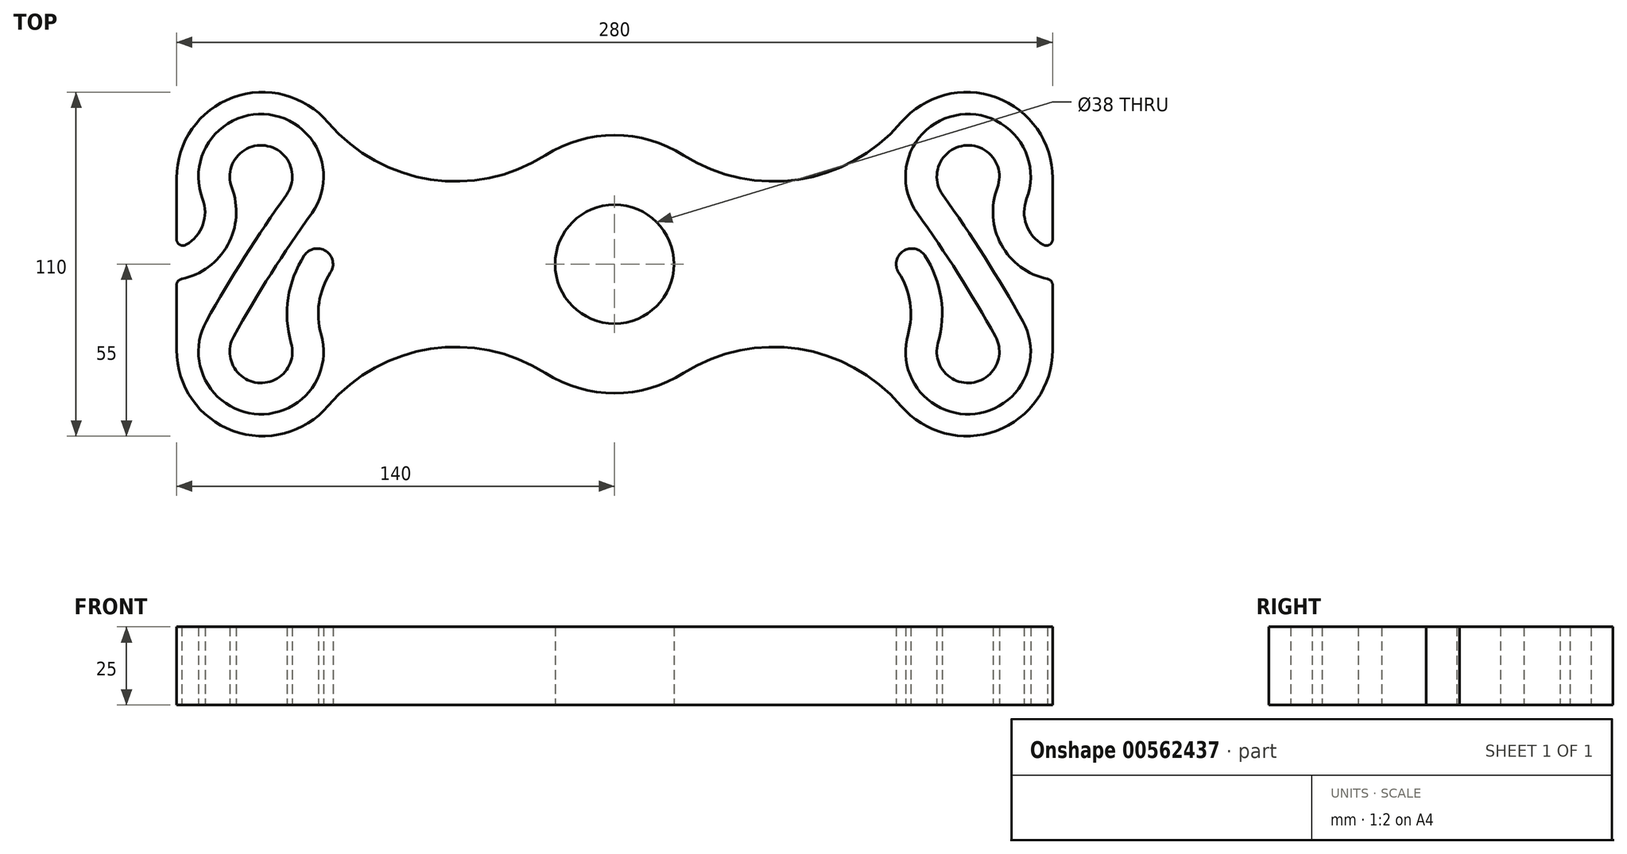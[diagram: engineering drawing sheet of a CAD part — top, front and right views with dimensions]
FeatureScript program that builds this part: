
annotation { "Feature Type Name" : "Feature", "Feature Type Description" : "" }
export const myFeature = defineFeature(function(context is Context, id is Id, definition is map)
    precondition{}
    {
        {
            var Q0;
            Q0=qCreatedBy(makeId("Top.planeOp"),FACE);
            var sketch = newSketch(context, id + "F0", { "sketchPlane" : qUnion([Q0])});
            skLineSegment(sketch, "E0.bottom", {"start": v(0, 0) * mm, "end": v(280, 0) * mm, "construction": true});
            skLineSegment(sketch, "E0.top", {"start": v(0, 110) * mm, "end": v(280, 110) * mm, "construction": true});
            skLineSegment(sketch, "E0.left", {"start": v(0, 0) * mm, "end": v(0, 110) * mm, "construction": true});
            skLineSegment(sketch, "E0.right", {"start": v(280, 0) * mm, "end": v(280, 110) * mm, "construction": true});
            skArc(sketch, "E1", {"start": v(140, 74) * mm, "mid": v(121, 55) * mm, "end": v(140, 36) * mm});
            skPoint(sketch, "E1.centerSnap0", {"position": v(0, 55) * mm});
            skPoint(sketch, "E1.centerSnap1", {"position": v(140, 110) * mm});
            skCircle(sketch, "E2", {"center": v(140, 55) * mm, "radius": 55 * mm, "construction": true});
            skLineSegment(sketch, "E3", {"start": v(0, 55) * mm, "end": v(280, 55) * mm, "construction": true});
            skArc(sketch, "E4", {"start": v(48.44, 100.32) * mm, "mid": v(18, 108.3) * mm, "end": v(0, 82.5) * mm});
            skLineSegment(sketch, "E5", {"start": v(140, 110) * mm, "end": v(140, 0) * mm, "construction": true});
            skCircle(sketch, "E6.MirrorC", {"center": v(252.5, 82.5) * mm, "radius": 27.5 * mm, "construction": true});
            skLineSegment(sketch, "E7.MirrorCS", {"start": v(280, 55) * mm, "end": v(0, 55) * mm, "construction": true});
            skCircle(sketch, "E8.MirrorC", {"center": v(252.5, 27.5) * mm, "radius": 27.5 * mm, "construction": true});
            skArc(sketch, "E9", {"start": v(48.44, 100.32) * mm, "mid": v(81.2, 82.09) * mm, "end": v(117.89, 89.82) * mm});
            skArc(sketch, "E10", {"start": v(117.89, 20.18) * mm, "mid": v(128.49, 15.39) * mm, "end": v(140, 13.75) * mm});
            skArc(sketch, "E11.MirrorC", {"start": v(48.44, 9.68) * mm, "mid": v(81.2, 27.91) * mm, "end": v(117.89, 20.18) * mm});
            skArc(sketch, "E12.MirrorC", {"start": v(231.56, 100.32) * mm, "mid": v(198.8, 82.09) * mm, "end": v(162.11, 89.82) * mm, "construction": true});
            skArc(sketch, "E13.MirrorC", {"start": v(231.56, 9.68) * mm, "mid": v(198.8, 27.91) * mm, "end": v(162.11, 20.18) * mm, "construction": true});
            skArc(sketch, "E14", {"start": v(49.19, 52.27) * mm, "mid": v(47.73, 59.19) * mm, "end": v(40.81, 57.73) * mm});
            skCircle(sketch, "E15.MirrorC", {"center": v(235, 55) * mm, "radius": 5 * mm, "construction": true});
            skArc(sketch, "E16.trimOffspring", {"start": v(48.44, 9.68) * mm, "mid": v(18, 1.7) * mm, "end": v(0, 27.5) * mm});
            skLineSegment(sketch, "E17", {"start": v(0, 82.5) * mm, "end": v(0, 60) * mm, "construction": true});
            skArc(sketch, "E18", {"start": v(0, 50) * mm, "mid": v(0.82, 50.07) * mm, "end": v(1.63, 50.27) * mm});
            skArc(sketch, "E19", {"start": v(35.13, 77.17) * mm, "mid": v(28.3, 92.92) * mm, "end": v(17.65, 79.45) * mm});
            skArc(sketch, "E20.0", {"start": v(43.25, 71.35) * mm, "mid": v(29.58, 102.83) * mm, "end": v(8.3, 75.9) * mm});
            skArc(sketch, "E21.MirrorC", {"start": v(46.22, 32.52) * mm, "mid": v(24.74, 7.13) * mm, "end": v(9.51, 36.7) * mm});
            skArc(sketch, "E22.MirrorC", {"start": v(36.61, 29.76) * mm, "mid": v(25.87, 17.06) * mm, "end": v(18.26, 31.85) * mm});
            skArc(sketch, "E23", {"start": v(0, 60) * mm, "mid": v(7.72, 66.09) * mm, "end": v(8.3, 75.9) * mm});
            skArc(sketch, "E24", {"start": v(0, 50) * mm, "mid": v(15.96, 60.45) * mm, "end": v(17.65, 79.45) * mm});
            skArc(sketch, "E25", {"start": v(35.13, 77.17) * mm, "mid": v(21.73, 57.3) * mm, "end": v(9.51, 36.7) * mm});
            skArc(sketch, "E26.0", {"start": v(43.25, 71.35) * mm, "mid": v(30.18, 51.96) * mm, "end": v(18.26, 31.85) * mm});
            skLineSegment(sketch, "E27.trimOffspring", {"start": v(0, 50) * mm, "end": v(0, 27.5) * mm, "construction": true});
            skArc(sketch, "E28.trimOffspring", {"start": v(140, 96.25) * mm, "mid": v(128.49, 94.61) * mm, "end": v(117.89, 89.82) * mm});
            skArc(sketch, "E29.trimOffspring", {"start": v(162.11, 20.18) * mm, "mid": v(181.25, 55) * mm, "end": v(162.11, 89.82) * mm, "construction": true});
            skLineSegment(sketch, "E30", {"start": v(140, 96.25) * mm, "end": v(140, 74) * mm});
            skLineSegment(sketch, "E31", {"start": v(140, 36) * mm, "end": v(140, 13.75) * mm});
            skLineSegment(sketch, "E32", {"start": v(0, 82.5) * mm, "end": v(0, 60) * mm});
            skLineSegment(sketch, "E33", {"start": v(0, 50) * mm, "end": v(0, 27.5) * mm});
            skArc(sketch, "E34", {"start": v(40.81, 57.73) * mm, "mid": v(35.67, 44.2) * mm, "end": v(36.61, 29.76) * mm});
            skArc(sketch, "E35.0", {"start": v(49.19, 52.27) * mm, "mid": v(45.55, 42.72) * mm, "end": v(46.22, 32.52) * mm});
            skSolve(sketch);
        }
        {
            var Q0;
            Q0=makeQuery(id+"F0.imprint","IMPRINT",FACE,{"disambiguationData":[TD([[makeQuery(id+"F0.imprint","IMPRINT",EDGE,{"derivedFrom":sQuery(id+"F0.wireOp",EDGE,"E1")}),-1.0]])]});
            extrude(context, id + "F1", {"entities" : qUnion([Q0]), "depth" : 25 * mm, "offsetDistance" : 25 * mm});
        }
        {
            var Q0;
            Q0=makeQuery(id+"F1.opExtrude","SWEPT_BODY",BODY,{"disambiguationData":[OSD([sQuery(id+"F0.wireOp",EDGE,"E1"),sQuery(id+"F0.wireOp",EDGE,"E4"),sQuery(id+"F0.wireOp",EDGE,"E9"),sQuery(id+"F0.wireOp",EDGE,"E10"),sQuery(id+"F0.wireOp",EDGE,"E11.MirrorC"),sQuery(id+"F0.wireOp",EDGE,"E14"),sQuery(id+"F0.wireOp",EDGE,"E16.trimOffspring"),sQuery(id+"F0.wireOp",EDGE,"E18"),sQuery(id+"F0.wireOp",EDGE,"E19"),sQuery(id+"F0.wireOp",EDGE,"E20.0"),sQuery(id+"F0.wireOp",EDGE,"E21.MirrorC"),sQuery(id+"F0.wireOp",EDGE,"E22.MirrorC"),sQuery(id+"F0.wireOp",EDGE,"E23"),sQuery(id+"F0.wireOp",EDGE,"E24"),sQuery(id+"F0.wireOp",EDGE,"E25"),sQuery(id+"F0.wireOp",EDGE,"E26.0"),sQuery(id+"F0.wireOp",EDGE,"E28.trimOffspring"),sQuery(id+"F0.wireOp",EDGE,"E30"),sQuery(id+"F0.wireOp",EDGE,"E31"),sQuery(id+"F0.wireOp",EDGE,"E32"),sQuery(id+"F0.wireOp",EDGE,"E33"),sQuery(id+"F0.wireOp",EDGE,"E34"),sQuery(id+"F0.wireOp",EDGE,"E35.0")])]});
            var Q1;
            Q1=makeQuery(id+"F1.opExtrude","SWEPT_FACE",FACE,{"disambiguationData":[OSD([sQuery(id+"F0.wireOp",EDGE,"E30")])]});
            mirror(context, id + "F2", {"operationType" : NewBodyOperationType.ADD, "entities" : qUnion([Q0]), "mirrorPlane" : qUnion([Q1])});
        }
        {
            var Q0;
            Q0=makeQuery(id+"F1.opExtrude","SWEPT_EDGE",EDGE,{"disambiguationData":[OSD([sQuery(id+"F0.wireOp",EDGE,"E23"),sQuery(id+"F0.wireOp",EDGE,"E32")])]});
            var Q1;
            Q1=makeQuery(id+"F1.opExtrude","SWEPT_EDGE",EDGE,{"disambiguationData":[OSD([sQuery(id+"F0.wireOp",EDGE,"E18"),sQuery(id+"F0.wireOp",EDGE,"E24"),sQuery(id+"F0.wireOp",EDGE,"E33")])]});
            var Q2;
            Q2=makeQuery(id+"F2.opPattern","COPY",EDGE,{"derivedFrom":makeQuery(id+"F1.opExtrude","SWEPT_EDGE",EDGE,{"disambiguationData":[OSD([sQuery(id+"F0.wireOp",EDGE,"E23"),sQuery(id+"F0.wireOp",EDGE,"E32")])]}),"instanceName":"1"});
            var Q3;
            Q3=makeQuery(id+"F2.opPattern","COPY",EDGE,{"derivedFrom":makeQuery(id+"F1.opExtrude","SWEPT_EDGE",EDGE,{"disambiguationData":[OSD([sQuery(id+"F0.wireOp",EDGE,"E18"),sQuery(id+"F0.wireOp",EDGE,"E24"),sQuery(id+"F0.wireOp",EDGE,"E33")])]}),"instanceName":"1"});
            fillet(context, id + "F3", {"entities" : qUnion([Q0, Q1, Q2, Q3]), "radius" : 2 * mm, "tangentPropagation" : true, "allowEdgeOverflow" : false});
        }
    });
